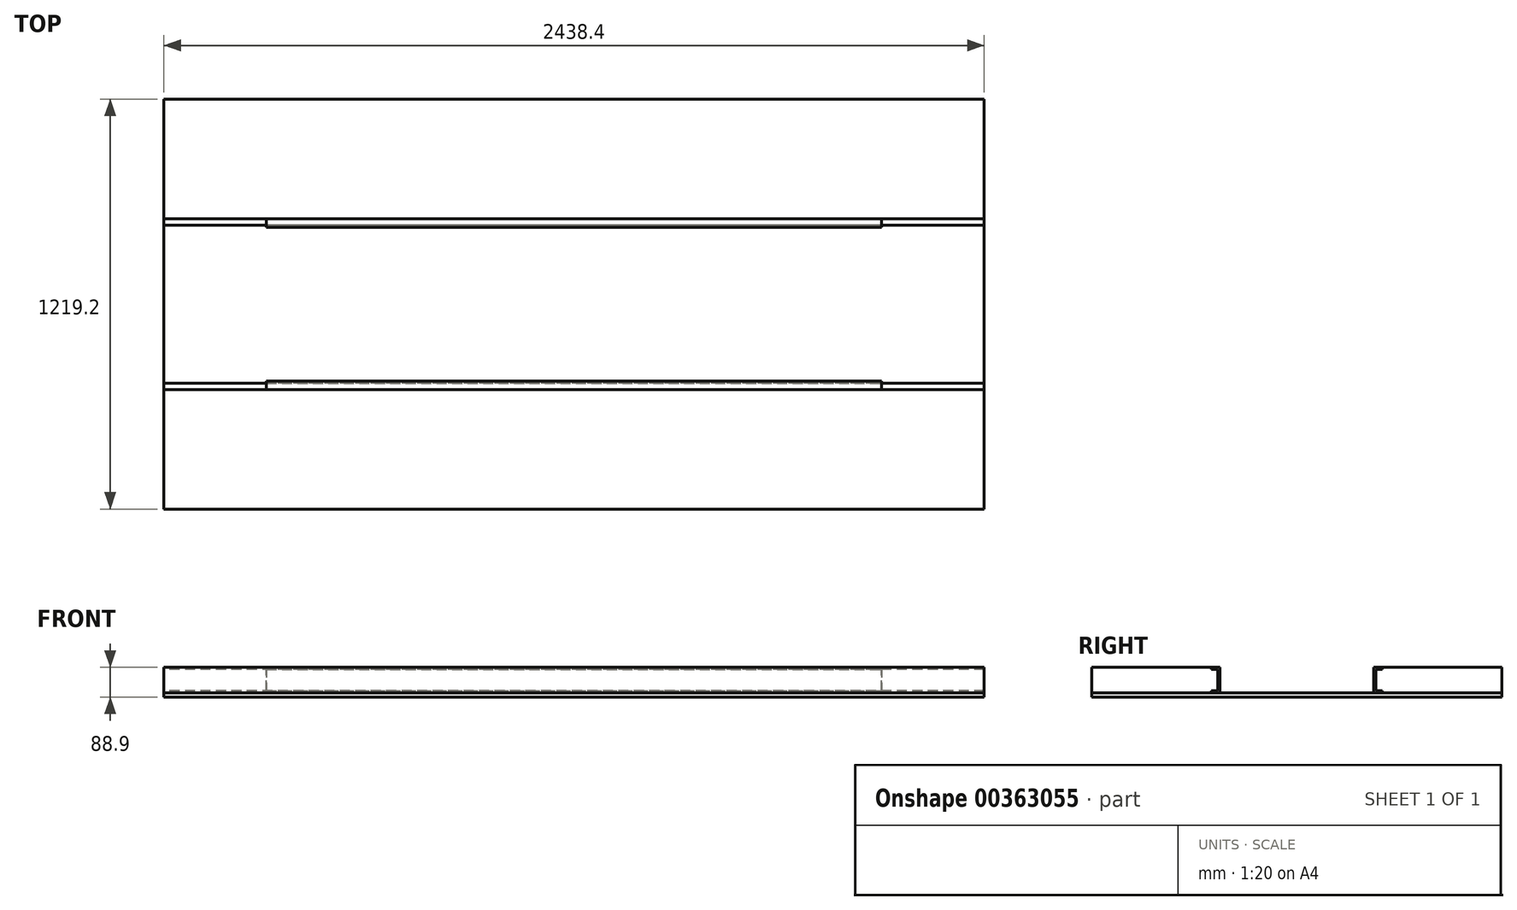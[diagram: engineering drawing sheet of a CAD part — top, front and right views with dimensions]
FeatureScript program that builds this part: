
annotation { "Feature Type Name" : "Feature", "Feature Type Description" : "" }
export const myFeature = defineFeature(function(context is Context, id is Id, definition is map)
    precondition{}
    {
        {
            var Q0;
            Q0=qCreatedBy(makeId("Top.planeOp"),FACE);
            var sketch = newSketch(context, id + "F0", { "sketchPlane" : qUnion([Q0])});
            skLineSegment(sketch, "E0.bottom", {"start": v(-1219.2, 609.6) * mm, "end": v(1219.2, 609.6) * mm});
            skLineSegment(sketch, "E0.top", {"start": v(-1219.2, -609.6) * mm, "end": v(1219.2, -609.6) * mm});
            skLineSegment(sketch, "E0.left", {"start": v(-1219.2, 609.6) * mm, "end": v(-1219.2, -609.6) * mm});
            skLineSegment(sketch, "E0.right", {"start": v(1219.2, 609.6) * mm, "end": v(1219.2, -609.6) * mm});
            skPoint(sketch, "E0.middle", {"position": v(0, 0) * mm});
            skSolve(sketch);
        }
        {
            var Q0;
            Q0=makeQuery(id+"F0.imprint","IMPRINT",FACE,{"disambiguationData":[TD([[makeQuery(id+"F0.imprint","IMPRINT",EDGE,{"derivedFrom":sQuery(id+"F0.wireOp",EDGE,"E0.bottom")}),-1.0]])]});
            extrude(context, id + "F1", {"entities" : qUnion([Q0]), "depth" : 12.7 * mm});
        }
        {
            var Q0;
            Q0=makeQuery(id+"F1.opExtrude","CAP_FACE",FACE,{"disambiguationData":[OSD([sQuery(id+"F0.wireOp",EDGE,"E0.bottom"),sQuery(id+"F0.wireOp",EDGE,"E0.top"),sQuery(id+"F0.wireOp",EDGE,"E0.left"),sQuery(id+"F0.wireOp",EDGE,"E0.right")])],"isStart":false});
            var sketch = newSketch(context, id + "F2", { "sketchPlane" : qUnion([Q0])});
            skLineSegment(sketch, "E1.bottom", {"start": v(-1219.2, 609.6) * mm, "end": v(1219.2, 609.6) * mm});
            skLineSegment(sketch, "E1.top", {"start": v(-1219.2, 228.6) * mm, "end": v(1219.2, 228.6) * mm});
            skLineSegment(sketch, "E1.left", {"start": v(-1219.2, 609.6) * mm, "end": v(-1219.2, 228.6) * mm});
            skLineSegment(sketch, "E1.right", {"start": v(1219.2, 609.6) * mm, "end": v(1219.2, 228.6) * mm});
            skLineSegment(sketch, "E2.bottom", {"start": v(-1219.2, -609.6) * mm, "end": v(1219.2, -609.6) * mm});
            skLineSegment(sketch, "E2.top", {"start": v(-1219.2, -228.6) * mm, "end": v(1219.2, -228.6) * mm});
            skLineSegment(sketch, "E2.left", {"start": v(-1219.2, -609.6) * mm, "end": v(-1219.2, -228.6) * mm});
            skLineSegment(sketch, "E2.right", {"start": v(1219.2, -609.6) * mm, "end": v(1219.2, -228.6) * mm});
            skSolve(sketch);
        }
        {
            var Q0;
            Q0 = qSketchRegion(id + "F2", true);
            extrude(context, id + "F3", {"entities" : qUnion([Q0]), "depth" : 76.2 * mm});
        }
        {
            var Q0;
            Q0=makeQuery(id+"F3.opExtrude","SWEPT_FACE",FACE,{"disambiguationData":[OSD([sQuery(id+"F2.wireOp",EDGE,"E1.left")])]});
            var sketch = newSketch(context, id + "F4", { "sketchPlane" : qUnion([Q0])});
            skLineSegment(sketch, "E3", {"start": v(-254, 88.9) * mm, "end": v(-254, 82.55) * mm});
            skLineSegment(sketch, "E4", {"start": v(-254, 82.55) * mm, "end": v(-234.95, 82.55) * mm});
            skLineSegment(sketch, "E5", {"start": v(-234.95, 82.55) * mm, "end": v(-234.95, 19.05) * mm});
            skLineSegment(sketch, "E6", {"start": v(-234.95, 19.05) * mm, "end": v(-254, 19.05) * mm});
            skLineSegment(sketch, "E7", {"start": v(-254, 19.05) * mm, "end": v(-254, 12.7) * mm});
            skLineSegment(sketch, "E8", {"start": v(-254, 12.7) * mm, "end": v(-228.6, 12.7) * mm});
            skLineSegment(sketch, "E9", {"start": v(-228.6, 12.7) * mm, "end": v(-228.6, 88.9) * mm});
            skLineSegment(sketch, "E10", {"start": v(-228.6, 88.9) * mm, "end": v(-254, 88.9) * mm});
            skLineSegment(sketch, "E11", {"start": v(0, 0) * mm, "end": v(0, 127.3) * mm, "construction": true});
            skLineSegment(sketch, "E12.MirrorCS", {"start": v(254, 88.9) * mm, "end": v(254, 82.55) * mm});
            skLineSegment(sketch, "E13.MirrorCS", {"start": v(254, 19.05) * mm, "end": v(254, 12.7) * mm});
            skLineSegment(sketch, "E14.MirrorCS", {"start": v(234.95, 82.55) * mm, "end": v(234.95, 19.05) * mm});
            skLineSegment(sketch, "E15.MirrorCS", {"start": v(254, 82.55) * mm, "end": v(234.95, 82.55) * mm});
            skLineSegment(sketch, "E16.MirrorCS", {"start": v(234.95, 19.05) * mm, "end": v(254, 19.05) * mm});
            skLineSegment(sketch, "E17.MirrorCS", {"start": v(228.6, 12.7) * mm, "end": v(228.6, 88.9) * mm});
            skLineSegment(sketch, "E18.MirrorCS", {"start": v(228.6, 88.9) * mm, "end": v(254, 88.9) * mm});
            skLineSegment(sketch, "E19.MirrorCS", {"start": v(254, 12.7) * mm, "end": v(228.6, 12.7) * mm});
            skSolve(sketch);
        }
        {
            var Q0;
            Q0=makeQuery(id+"F4.imprint","IMPRINT",FACE,{"disambiguationData":[TD([[makeQuery(id+"F4.imprint","IMPRINT",EDGE,{"derivedFrom":sQuery(id+"F4.wireOp",EDGE,"E3")}),1.0]])]});
            var Q1;
            Q1=makeQuery(id+"F4.imprint","IMPRINT",FACE,{"disambiguationData":[TD([[makeQuery(id+"F4.imprint","IMPRINT",EDGE,{"derivedFrom":sQuery(id+"F4.wireOp",EDGE,"E13.MirrorCS")}),-1.0]])]});
            extrude(context, id + "F5", {"entities" : qUnion([Q0, Q1]), "operationType" : NewBodyOperationType.REMOVE, "endBound" : BoundingType.THROUGH_ALL, "oppositeDirection" : true, "depth" : 25.4 * mm});
        }
        {
            var Q0;
            Q0=qCreatedBy(makeId("Right.planeOp"),FACE);
            var sketch = newSketch(context, id + "F6", { "sketchPlane" : qUnion([Q0])});
            skLineSegment(sketch, "E20", {"start": v(254, 88.9) * mm, "end": v(228.6, 88.9) * mm});
            skLineSegment(sketch, "E21", {"start": v(228.6, 88.9) * mm, "end": v(228.6, 12.7) * mm});
            skLineSegment(sketch, "E22", {"start": v(228.6, 12.7) * mm, "end": v(254, 12.7) * mm});
            skLineSegment(sketch, "E23", {"start": v(254, 12.7) * mm, "end": v(254, 19.05) * mm});
            skLineSegment(sketch, "E24", {"start": v(254, 19.05) * mm, "end": v(234.95, 19.05) * mm});
            skLineSegment(sketch, "E25", {"start": v(234.95, 19.05) * mm, "end": v(234.95, 82.55) * mm});
            skLineSegment(sketch, "E26", {"start": v(234.95, 82.55) * mm, "end": v(254, 82.55) * mm});
            skLineSegment(sketch, "E27", {"start": v(254, 82.55) * mm, "end": v(254, 88.9) * mm});
            skLineSegment(sketch, "E28", {"start": v(0, 0) * mm, "end": v(0, 110.92) * mm, "construction": true});
            skLineSegment(sketch, "E29.MirrorCS", {"start": v(-254, 88.9) * mm, "end": v(-228.6, 88.9) * mm});
            skLineSegment(sketch, "E30.MirrorCS", {"start": v(-228.6, 88.9) * mm, "end": v(-228.6, 12.7) * mm});
            skLineSegment(sketch, "E31.MirrorCS", {"start": v(-254, 12.7) * mm, "end": v(-254, 19.05) * mm});
            skLineSegment(sketch, "E32.MirrorCS", {"start": v(-254, 19.05) * mm, "end": v(-234.95, 19.05) * mm});
            skLineSegment(sketch, "E33.MirrorCS", {"start": v(-228.6, 12.7) * mm, "end": v(-254, 12.7) * mm});
            skLineSegment(sketch, "E34.MirrorCS", {"start": v(-254, 82.55) * mm, "end": v(-254, 88.9) * mm});
            skLineSegment(sketch, "E35.MirrorCS", {"start": v(-234.95, 82.55) * mm, "end": v(-254, 82.55) * mm});
            skLineSegment(sketch, "E36.MirrorCS", {"start": v(-234.95, 19.05) * mm, "end": v(-234.95, 82.55) * mm});
            skSolve(sketch);
        }
        {
            var Q0;
            Q0=makeQuery(id+"F6.imprint","IMPRINT",FACE,{"disambiguationData":[TD([[makeQuery(id+"F6.imprint","IMPRINT",EDGE,{"derivedFrom":sQuery(id+"F6.wireOp",EDGE,"E20")}),1.0]])]});
            var Q1;
            Q1=makeQuery(id+"F6.imprint","IMPRINT",FACE,{"disambiguationData":[TD([[makeQuery(id+"F6.imprint","IMPRINT",EDGE,{"derivedFrom":sQuery(id+"F6.wireOp",EDGE,"E29.MirrorCS")}),-1.0]])]});
            var Q2;
            Q2=makeQuery(id+"F3.opExtrude","SWEPT_FACE",FACE,{"disambiguationData":[OSD([sQuery(id+"F2.wireOp",EDGE,"E1.left")])]});
            extrude(context, id + "F7", {"entities" : qUnion([Q0, Q1]), "endBound" : BoundingType.SYMMETRIC, "oppositeDirection" : true, "endBoundEntityFace" : qUnion([Q2]), "depth" : 1828.8 * mm});
        }
    });
